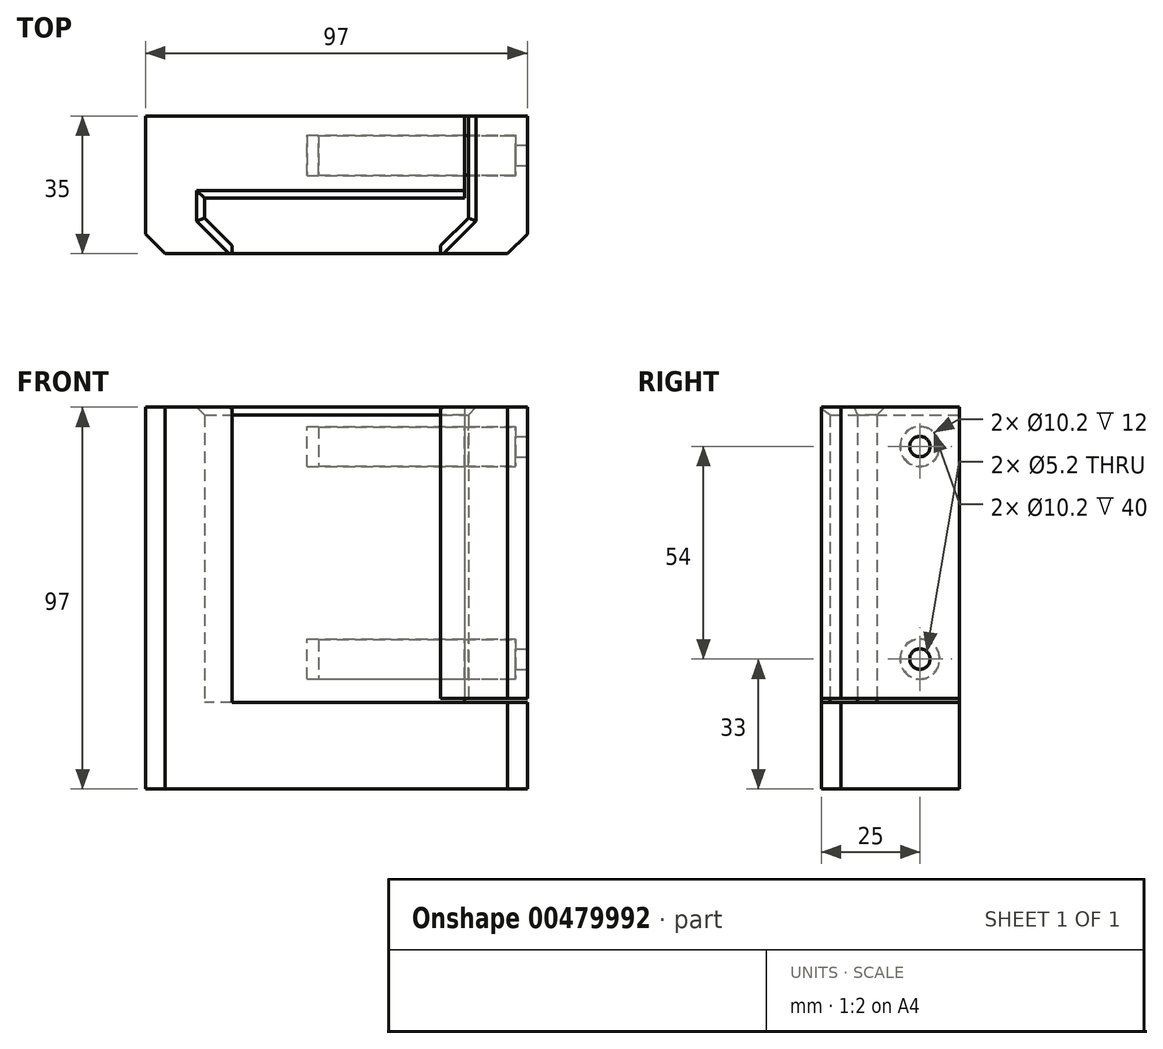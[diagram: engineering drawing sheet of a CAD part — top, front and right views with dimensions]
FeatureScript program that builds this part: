
annotation { "Feature Type Name" : "Feature", "Feature Type Description" : "" }
export const myFeature = defineFeature(function(context is Context, id is Id, definition is map)
    precondition{}
    {
        {
            var Q0;
            Q0=qCreatedBy(makeId("Top.planeOp"),FACE);
            var sketch = newSketch(context, id + "F0", { "sketchPlane" : qUnion([Q0])});
            skPoint(sketch, "E0.middle", {"position": v(0, 0) * mm});
            skLineSegment(sketch, "E1", {"start": v(-26.5, -12.91) * mm, "end": v(-33.5, -5.91) * mm});
            skLineSegment(sketch, "E2", {"start": v(-33.5, -0.91) * mm, "end": v(-33.5, -5.91) * mm});
            skLineSegment(sketch, "E3", {"start": v(-26.5, -15) * mm, "end": v(-26.5, -12.91) * mm});
            skLineSegment(sketch, "E4.MirrorCS", {"start": v(26.5, -15) * mm, "end": v(26.5, -12.91) * mm});
            skLineSegment(sketch, "E5.MirrorCS", {"start": v(26.5, -12.91) * mm, "end": v(33.5, -5.91) * mm});
            skPoint(sketch, "E6.MirrorP", {"position": v(26.5, -15) * mm});
            skLineSegment(sketch, "E7", {"start": v(-33.5, -0.91) * mm, "end": v(32.5, -0.91) * mm});
            skLineSegment(sketch, "E8", {"start": v(-48.5, -15) * mm, "end": v(-48.5, 20) * mm});
            skLineSegment(sketch, "E9", {"start": v(-48.5, -15) * mm, "end": v(-26.5, -15) * mm});
            skLineSegment(sketch, "E10", {"start": v(-48.5, 20) * mm, "end": v(32.5, 20) * mm});
            skLineSegment(sketch, "E11", {"start": v(32.5, 20) * mm, "end": v(32.5, -0.91) * mm});
            skLineSegment(sketch, "E12", {"start": v(33.5, -5.91) * mm, "end": v(33.5, 20) * mm});
            skLineSegment(sketch, "E13", {"start": v(33.5, 20) * mm, "end": v(48.5, 20) * mm});
            skLineSegment(sketch, "E14", {"start": v(48.5, 20) * mm, "end": v(48.5, -15) * mm});
            skLineSegment(sketch, "E15", {"start": v(26.5, -15) * mm, "end": v(48.5, -15) * mm});
            skSolve(sketch);
        }
        {
            var Q0;
            Q0=makeQuery(id+"F0.imprint","IMPRINT",FACE,{"disambiguationData":[TD([[makeQuery(id+"F0.imprint","IMPRINT",EDGE,{"derivedFrom":sQuery(id+"F0.wireOp",EDGE,"E0.right")}),1.0]])]});
            var Q1;
            Q1=makeQuery(id+"F0.imprint","IMPRINT",FACE,{"disambiguationData":[TD([[makeQuery(id+"F0.imprint","IMPRINT",EDGE,{"derivedFrom":sQuery(id+"F0.wireOp",EDGE,"E1")}),1.0]])]});
            extrude(context, id + "F1", {"entities" : qUnion([Q0, Q1]), "endBound" : BoundingType.SYMMETRIC, "depth" : 75 * mm});
        }
        {
            var Q0;
            Q0=makeQuery(id+"F0.imprint","IMPRINT",FACE,{"disambiguationData":[TD([[makeQuery(id+"F0.imprint","IMPRINT",EDGE,{"derivedFrom":sQuery(id+"F0.wireOp",EDGE,"E4.MirrorCS")}),-1.0]])]});
            var Q1;
            Q1=makeQuery(id+"F1.opExtrude","CAP_FACE",FACE,{"disambiguationData":[OSD([sQuery(id+"F0.wireOp",EDGE,"E1"),sQuery(id+"F0.wireOp",EDGE,"E2"),sQuery(id+"F0.wireOp",EDGE,"E3"),sQuery(id+"F0.wireOp",EDGE,"E7"),sQuery(id+"F0.wireOp",EDGE,"E8"),sQuery(id+"F0.wireOp",EDGE,"E9"),sQuery(id+"F0.wireOp",EDGE,"E10"),sQuery(id+"F0.wireOp",EDGE,"E11")])],"isStart":false});
            extrude(context, id + "F2", {"entities" : qUnion([Q0]), "endBound" : BoundingType.UP_TO_SURFACE, "endBoundEntityFace" : qUnion([Q1]), "depth" : 74 * mm, "hasSecondDirection" : true, "secondDirectionOppositeDirection" : true, "secondDirectionDepth" : 36.5 * mm});
        }
        {
            var Q0;
            Q0=makeQuery(id+"F1.opExtrude","CAP_FACE",FACE,{"disambiguationData":[OSD([sQuery(id+"F0.wireOp",EDGE,"E1"),sQuery(id+"F0.wireOp",EDGE,"E2"),sQuery(id+"F0.wireOp",EDGE,"E3"),sQuery(id+"F0.wireOp",EDGE,"E7"),sQuery(id+"F0.wireOp",EDGE,"E8"),sQuery(id+"F0.wireOp",EDGE,"E9"),sQuery(id+"F0.wireOp",EDGE,"E10"),sQuery(id+"F0.wireOp",EDGE,"E11")])],"isStart":true});
            var sketch = newSketch(context, id + "F3", { "sketchPlane" : qUnion([Q0])});
            skLineSegment(sketch, "E16", {"start": v(-48.5, 15) * mm, "end": v(-48.5, -20) * mm});
            skLineSegment(sketch, "E17.MirrorCS", {"start": v(48.5, 15) * mm, "end": v(48.5, -20) * mm});
            skLineSegment(sketch, "E18", {"start": v(-48.5, 15) * mm, "end": v(48.5, 15) * mm});
            skLineSegment(sketch, "E19", {"start": v(48.5, -20) * mm, "end": v(-48.5, -20) * mm});
            skSolve(sketch);
        }
        {
            var Q0;
            Q0 = qSketchRegion(id + "F3", true);
            extrude(context, id + "F4", {"entities" : qUnion([Q0]), "operationType" : NewBodyOperationType.ADD, "depth" : 22 * mm});
        }
        {
            var Q0;
            Q0=makeQuery(id+"F4.boolean.opBoolean","MERGE",EDGE,{"derivedFrom":[makeQuery(id+"F1.opExtrude","SWEPT_EDGE",EDGE,{"disambiguationData":[OSD([sQuery(id+"F0.wireOp",EDGE,"E8"),sQuery(id+"F0.wireOp",EDGE,"E9")])]}),makeQuery(id+"F4.opExtrude","SWEPT_EDGE",EDGE,{"disambiguationData":[OSD([sQuery(id+"F3.wireOp",EDGE,"E16"),sQuery(id+"F3.wireOp",EDGE,"E18")])]})]});
            var Q1;
            Q1=makeQuery(id+"F2.opExtrude","SWEPT_EDGE",EDGE,{"disambiguationData":[OSD([sQuery(id+"F0.wireOp",EDGE,"E14"),sQuery(id+"F0.wireOp",EDGE,"E15")])]});
            var Q2;
            Q2=makeQuery(id+"F4.opExtrude","SWEPT_EDGE",EDGE,{"disambiguationData":[OSD([sQuery(id+"F3.wireOp",EDGE,"E17.MirrorCS"),sQuery(id+"F3.wireOp",EDGE,"E18")])]});
            chamfer(context, id + "F5", {"entities" : qUnion([Q0, Q1, Q2]), "width" : 5 * mm, "tangentPropagation" : true});
        }
        {
            var Q0;
            Q0=makeQuery(id+"F2.opExtrude","SWEPT_FACE",FACE,{"disambiguationData":[OSD([sQuery(id+"F0.wireOp",EDGE,"E14")])]});
            var sketch = newSketch(context, id + "F6", { "sketchPlane" : qUnion([Q0])});
            skCircle(sketch, "E20", {"center": v(10, 27.5) * mm, "radius": 5.1 * mm});
            skCircle(sketch, "E21", {"center": v(10, -26.5) * mm, "radius": 5.1 * mm});
            skSolve(sketch);
        }
        {
            var Q0;
            Q0=makeQuery(id+"F6.imprint","IMPRINT",FACE,{"disambiguationData":[TD([[makeQuery(id+"F6.imprint","IMPRINT",EDGE,{"derivedFrom":sQuery(id+"F6.wireOp",EDGE,"E20")}),1.0]])]});
            var Q1;
            Q1=makeQuery(id+"F6.imprint","IMPRINT",FACE,{"disambiguationData":[TD([[makeQuery(id+"F6.imprint","IMPRINT",EDGE,{"derivedFrom":sQuery(id+"F6.wireOp",EDGE,"E21")}),1.0]])]});
            extrude(context, id + "F7", {"entities" : qUnion([Q0, Q1]), "operationType" : NewBodyOperationType.REMOVE, "oppositeDirection" : true, "depth" : 15 * mm, "hasSecondDirection" : true, "secondDirectionOppositeDirection" : true, "secondDirectionDepth" : 3 * mm});
        }
        {
            var Q0;
            Q0=makeQuery(id+"F2.opExtrude","SWEPT_FACE",FACE,{"disambiguationData":[OSD([sQuery(id+"F0.wireOp",EDGE,"E14")])]});
            var sketch = newSketch(context, id + "F8", { "sketchPlane" : qUnion([Q0])});
            skCircle(sketch, "E22", {"center": v(10, 27.5) * mm, "radius": 2.6 * mm});
            skCircle(sketch, "E23", {"center": v(10, -26.5) * mm, "radius": 2.6 * mm});
            skSolve(sketch);
        }
        {
            var Q0;
            Q0 = qSketchRegion(id + "F8", true);
            var Q1;
            Q1=sQuery(id+"F8.wireOp",EDGE,"E23");
            var Q2;
            Q2=sQuery(id+"F8.wireOp",EDGE,"E22");
            extrude(context, id + "F9", {"entities" : qUnion([Q0]), "operationType" : NewBodyOperationType.REMOVE, "surfaceEntities" : qUnion([Q1, Q2]), "oppositeDirection" : true, "depth" : 3 * mm});
        }
        {
            var Q0;
            Q0=makeQuery(id+"F1.opExtrude","SWEPT_FACE",FACE,{"disambiguationData":[OSD([sQuery(id+"F0.wireOp",EDGE,"E11")])]});
            var sketch = newSketch(context, id + "F10", { "sketchPlane" : qUnion([Q0])});
            skCircle(sketch, "E24", {"center": v(10, 27.5) * mm, "radius": 5.1 * mm});
            skCircle(sketch, "E25", {"center": v(10, -26.5) * mm, "radius": 5.1 * mm});
            skSolve(sketch);
        }
        {
            var Q0;
            Q0 = qSketchRegion(id + "F10", true);
            extrude(context, id + "F11", {"entities" : qUnion([Q0]), "operationType" : NewBodyOperationType.REMOVE, "oppositeDirection" : true, "depth" : 40 * mm});
        }
        {
            var Q0;
            Q0=makeQuery(id+"F7.boolean.opBoolean","COPY",FACE,{"derivedFrom":makeQuery(id+"F7.opExtrude","CAP_FACE",FACE,{"disambiguationData":[OSD([sQuery(id+"F6.wireOp",EDGE,"E20")])],"isStart":true})});
            var sketch = newSketch(context, id + "F12", { "sketchPlane" : qUnion([Q0])});
            skCircle(sketch, "E26", {"center": v(-10, 27.5) * mm, "radius": 5 * mm});
            skCircle(sketch, "E27", {"center": v(-10, -26.5) * mm, "radius": 5 * mm});
            skSolve(sketch);
        }
        {
            var Q0;
            Q0 = qSketchRegion(id + "F12", true);
            extrude(context, id + "F13", {"entities" : qUnion([Q0]), "depth" : 50 * mm});
        }
        {
            var Q0;
            Q0=makeQuery(id+"F1.opExtrude","CAP_EDGE",EDGE,{"disambiguationData":[OSD([sQuery(id+"F0.wireOp",EDGE,"E7")])],"isStart":false});
            var Q1;
            Q1=makeQuery(id+"F1.opExtrude","CAP_EDGE",EDGE,{"disambiguationData":[OSD([sQuery(id+"F0.wireOp",EDGE,"E2")])],"isStart":false});
            var Q2;
            Q2=makeQuery(id+"F1.opExtrude","CAP_EDGE",EDGE,{"disambiguationData":[OSD([sQuery(id+"F0.wireOp",EDGE,"E1")])],"isStart":false});
            var Q3;
            Q3=makeQuery(id+"F2.opExtrude","CAP_EDGE",EDGE,{"disambiguationData":[OSD([sQuery(id+"F0.wireOp",EDGE,"E5.MirrorCS")])],"isStart":false});
            var Q4;
            Q4=makeQuery(id+"F2.opExtrude","CAP_EDGE",EDGE,{"disambiguationData":[OSD([sQuery(id+"F0.wireOp",EDGE,"E12")])],"isStart":false});
            chamfer(context, id + "F14", {"entities" : qUnion([Q0, Q1, Q2, Q3, Q4]), "width" : 2 * mm, "tangentPropagation" : true});
        }
    });
